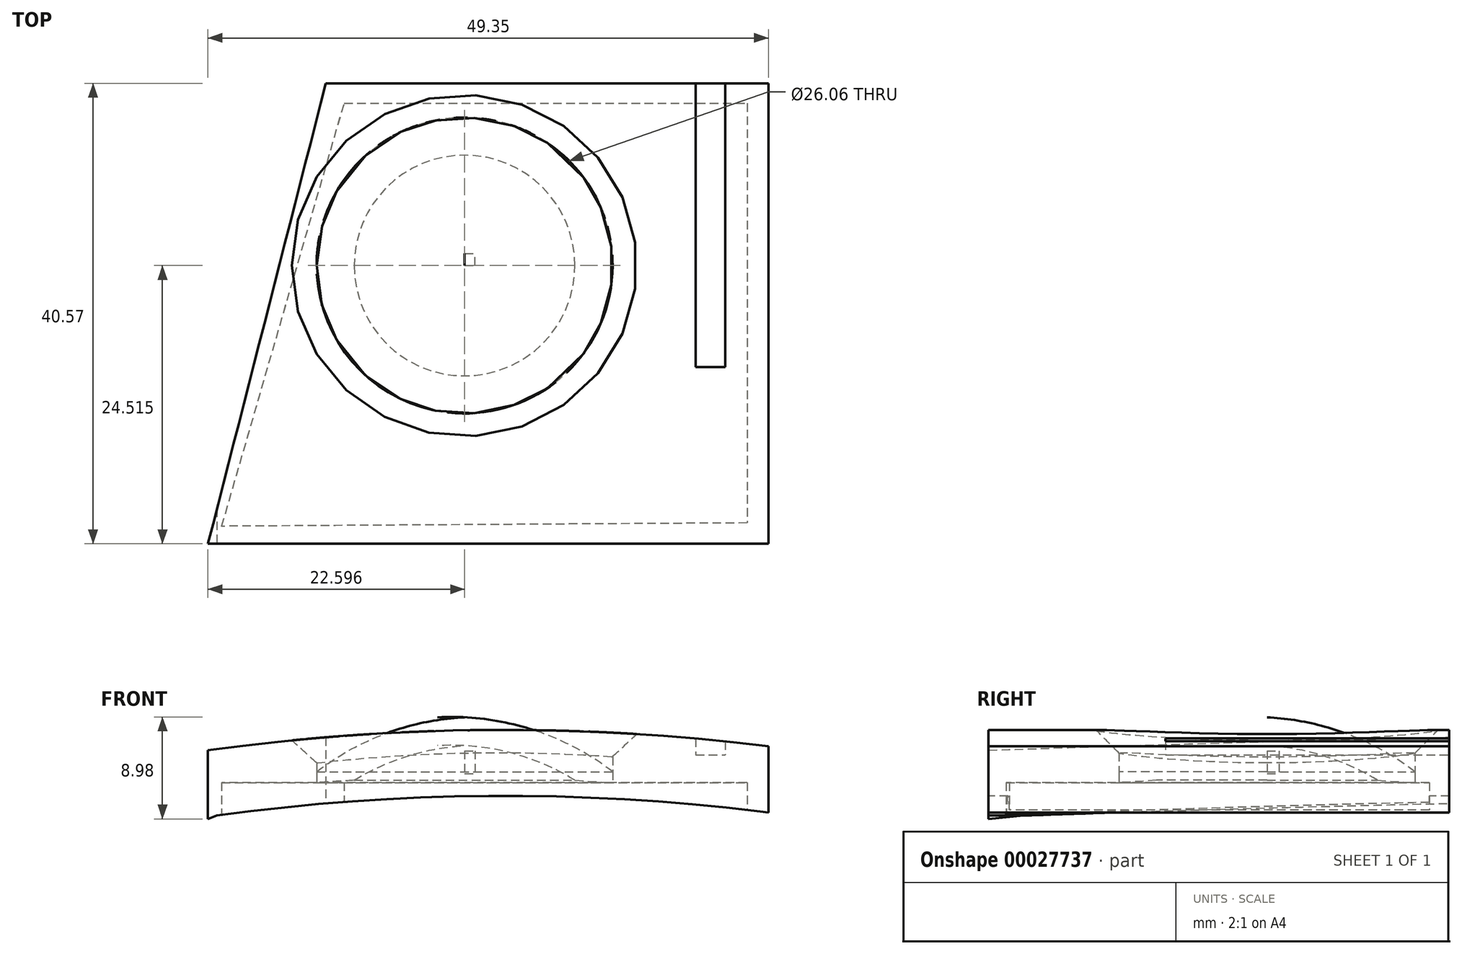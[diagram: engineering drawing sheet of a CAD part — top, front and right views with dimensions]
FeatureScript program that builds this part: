
annotation { "Feature Type Name" : "Feature", "Feature Type Description" : "" }
export const myFeature = defineFeature(function(context is Context, id is Id, definition is map)
    precondition{}
    {
        {
            var Q0;
            Q0=qCreatedBy(makeId("Top.planeOp"),FACE);
            var sketch = newSketch(context, id + "F0", { "sketchPlane" : qUnion([Q0])});
            skLineSegment(sketch, "E0", {"start": v(0, 0) * mm, "end": v(10.38, 40.57) * mm});
            skLineSegment(sketch, "E1", {"start": v(10.38, 40.57) * mm, "end": v(49.35, 40.57) * mm});
            skLineSegment(sketch, "E2", {"start": v(49.35, 40.57) * mm, "end": v(49.35, 0) * mm});
            skLineSegment(sketch, "E3", {"start": v(49.35, 0) * mm, "end": v(0, 0) * mm});
            skSolve(sketch);
        }
        {
            var Q0;
            Q0 = qSketchRegion(id + "F0", true);
            extrude(context, id + "F1", {"entities" : qUnion([Q0]), "depth" : 8 * mm});
        }
        {
            var Q0;
            Q0=makeQuery(id+"F1.opExtrude","SWEPT_FACE",FACE,{"disambiguationData":[OSD([sQuery(id+"F0.wireOp",EDGE,"E3")])]});
            var sketch = newSketch(context, id + "F2", { "sketchPlane" : qUnion([Q0])});
            skArc(sketch, "E4", {"start": v(49.35, 6.4) * mm, "mid": v(24.66, 7.83) * mm, "end": v(0, 6.04) * mm});
            skLineSegment(sketch, "E5", {"start": v(0, 6.04) * mm, "end": v(0, 8) * mm});
            skLineSegment(sketch, "E6", {"start": v(0, 8) * mm, "end": v(49.35, 8) * mm});
            skLineSegment(sketch, "E7", {"start": v(49.35, 8) * mm, "end": v(49.35, 6.4) * mm});
            skArc(sketch, "E8.0", {"start": v(48.64, 0.64) * mm, "mid": v(24.7, 2.03) * mm, "end": v(0.8, 0.3) * mm});
            skLineSegment(sketch, "E9", {"start": v(0.8, 0.3) * mm, "end": v(0, 0) * mm});
            skLineSegment(sketch, "E10", {"start": v(0, 0) * mm, "end": v(49.35, 0) * mm});
            skLineSegment(sketch, "E11", {"start": v(48.64, 0.64) * mm, "end": v(49.35, 0.56) * mm});
            skLineSegment(sketch, "E12", {"start": v(49.35, 0.56) * mm, "end": v(49.35, 0) * mm});
            skSolve(sketch);
        }
        {
            var Q0;
            Q0 = qSketchRegion(id + "F2", true);
            extrude(context, id + "F3", {"entities" : qUnion([Q0]), "operationType" : NewBodyOperationType.REMOVE, "endBound" : BoundingType.THROUGH_ALL, "oppositeDirection" : true, "depth" : 25 * mm});
        }
        {
            var Q0;
            Q0=qCreatedBy(makeId("Top.planeOp"),FACE);
            var sketch = newSketch(context, id + "F4", { "sketchPlane" : qUnion([Q0])});
            skCircle(sketch, "E13", {"center": v(22.6, 24.52) * mm, "radius": 13.03 * mm});
            skSolve(sketch);
        }
        {
            var Q0;
            Q0 = qSketchRegion(id + "F4", true);
            extrude(context, id + "F5", {"entities" : qUnion([Q0]), "operationType" : NewBodyOperationType.REMOVE, "endBound" : BoundingType.THROUGH_ALL, "depth" : 25 * mm});
        }
        {
            var Q0;
            Q0=makeQuery(id+"F5.boolean.opBoolean","INTERSECT",EDGE,{"derivedFrom":[makeQuery(id+"F3.boolean.opBoolean","COPY",FACE,{"derivedFrom":makeQuery(id+"F3.opExtrude","SWEPT_FACE",FACE,{"disambiguationData":[OSD([sQuery(id+"F2.wireOp",EDGE,"E4")])]})}),makeQuery(id+"F5.opExtrude","SWEPT_FACE",FACE,{"disambiguationData":[OSD([sQuery(id+"F4.wireOp",EDGE,"E13")])]})]});
            chamfer(context, id + "F6", {"entities" : qUnion([Q0]), "width" : 2 * mm, "tangentPropagation" : true});
        }
        {
            var Q0;
            Q0=makeQuery(id+"F1.opExtrude","SWEPT_FACE",FACE,{"disambiguationData":[OSD([sQuery(id+"F0.wireOp",EDGE,"E1")])]});
            var sketch = newSketch(context, id + "F7", { "sketchPlane" : qUnion([Q0])});
            skLineSegment(sketch, "E14.bottom", {"start": v(-42.95, 7.09) * mm, "end": v(-45.54, 7.09) * mm});
            skLineSegment(sketch, "E14.top", {"start": v(-42.95, 5.64) * mm, "end": v(-45.54, 5.64) * mm});
            skLineSegment(sketch, "E14.left", {"start": v(-42.95, 7.09) * mm, "end": v(-42.95, 5.64) * mm});
            skLineSegment(sketch, "E14.right", {"start": v(-45.54, 7.09) * mm, "end": v(-45.54, 5.64) * mm});
            skSolve(sketch);
        }
        {
            var Q0;
            Q0=makeQuery(id+"F1.opExtrude","SWEPT_FACE",FACE,{"disambiguationData":[OSD([sQuery(id+"F0.wireOp",EDGE,"E3")])]});
            var sketch = newSketch(context, id + "F8", { "sketchPlane" : qUnion([Q0])});
            skLineSegment(sketch, "E15", {"start": v(0, 0) * mm, "end": v(49.35, 0.56) * mm});
            skLineSegment(sketch, "E16", {"start": v(0, 0) * mm, "end": v(8.86, -24.08) * mm});
            skLineSegment(sketch, "E17", {"start": v(8.86, -24.08) * mm, "end": v(40.08, -26.42) * mm});
            skLineSegment(sketch, "E18", {"start": v(40.08, -26.42) * mm, "end": v(49.35, 0.56) * mm});
            skSolve(sketch);
        }
        {
            var Q0;
            Q0 = qSketchRegion(id + "F7", true);
            extrude(context, id + "F9", {"entities" : qUnion([Q0]), "operationType" : NewBodyOperationType.REMOVE, "oppositeDirection" : true, "depth" : 25 * mm});
        }
        {
            var Q0;
            Q0 = qSketchRegion(id + "F8", true);
            extrude(context, id + "F10", {"entities" : qUnion([Q0]), "operationType" : NewBodyOperationType.REMOVE, "endBound" : BoundingType.THROUGH_ALL, "oppositeDirection" : true, "depth" : 25 * mm});
        }
        {
            var Q0;
            Q0=qCreatedBy(makeId("Top.planeOp"),FACE);
            var sketch = newSketch(context, id + "F11", { "sketchPlane" : qUnion([Q0])});
            skLineSegment(sketch, "E19", {"start": v(1.2, 1.55) * mm, "end": v(12, 38.8) * mm});
            skLineSegment(sketch, "E20", {"start": v(12, 38.8) * mm, "end": v(47.48, 38.8) * mm});
            skLineSegment(sketch, "E21", {"start": v(47.48, 38.8) * mm, "end": v(47.48, 1.84) * mm});
            skLineSegment(sketch, "E22", {"start": v(47.48, 1.84) * mm, "end": v(1.2, 1.55) * mm});
            skSolve(sketch);
        }
        {
            var Q0;
            Q0 = qSketchRegion(id + "F11", true);
            extrude(context, id + "F12", {"entities" : qUnion([Q0]), "operationType" : NewBodyOperationType.REMOVE, "depth" : 3.2 * mm});
        }
        {
            var Q0;
            Q0=qCreatedBy(makeId("Top.planeOp"),FACE);
            cPlane(context, id + "F13", {"entities" : qUnion([Q0]), "cplaneType" : CPlaneType.OFFSET, "offset" : 4 * mm, "width" : 150 * mm, "height" : 150 * mm});
        }
        {
            var Q0;
            Q0=qCreatedBy(id+"F13.planeOp",FACE);
            var sketch = newSketch(context, id + "F14", { "sketchPlane" : qUnion([Q0])});
            skLineSegment(sketch, "E23.bottom", {"start": v(22.6, 24.52) * mm, "end": v(23.53, 24.52) * mm});
            skLineSegment(sketch, "E23.top", {"start": v(22.6, 25.56) * mm, "end": v(23.53, 25.56) * mm});
            skLineSegment(sketch, "E23.left", {"start": v(22.6, 24.52) * mm, "end": v(22.6, 25.56) * mm});
            skLineSegment(sketch, "E23.right", {"start": v(23.53, 24.52) * mm, "end": v(23.53, 25.56) * mm});
            skSolve(sketch);
        }
        {
            var Q0;
            Q0 = qSketchRegion(id + "F14", true);
            extrude(context, id + "F15", {"entities" : qUnion([Q0]), "depth" : 2 * mm});
        }
        {
            var Q0;
            Q0=makeQuery(id+"F15.opExtrude","SWEPT_FACE",FACE,{"disambiguationData":[OSD([sQuery(id+"F14.wireOp",EDGE,"E23.bottom")])]});
            var sketch = newSketch(context, id + "F16", { "sketchPlane" : qUnion([Q0])});
            skLineSegment(sketch, "E24", {"start": v(22.6, 4) * mm, "end": v(22.6, 8.07) * mm});
            skLineSegment(sketch, "E25", {"start": v(22.6, 8.07) * mm, "end": v(22.6, 8.95) * mm});
            skLineSegment(sketch, "E26", {"start": v(9.56, 3.2) * mm, "end": v(9.56, 5.1) * mm});
            skLineSegment(sketch, "E27", {"start": v(35.63, 5.66) * mm, "end": v(35.63, 3.2) * mm});
            skArc(sketch, "E28", {"start": v(22.6, 8.95) * mm, "mid": v(15.72, 7.55) * mm, "end": v(9.56, 4.15) * mm});
            skLineSegment(sketch, "E29", {"start": v(9.56, 3.2) * mm, "end": v(22.6, 4) * mm});
            skSolve(sketch);
        }
        {
            var Q0;
            Q0 = qSketchRegion(id + "F16", true);
            var Q1;
            Q1=sQuery(id+"F16.wireOp",EDGE,"E24");
            revolve(context, id + "F17", {"entities" : qUnion([Q0]), "axis" : qUnion([Q1]), "revolveType" : RevolveType.FULL});
        }
        {
            var Q0;
            Q0=makeQuery(id+"F17.opRevolve","SWEPT_FACE",FACE,{"disambiguationData":[OSD([sQuery(id+"F16.wireOp",EDGE,"E29")])]});
            shell(context, id + "F18", {"entities" : qUnion([Q0]), "thickness" : 2.5 * mm});
        }
    });
